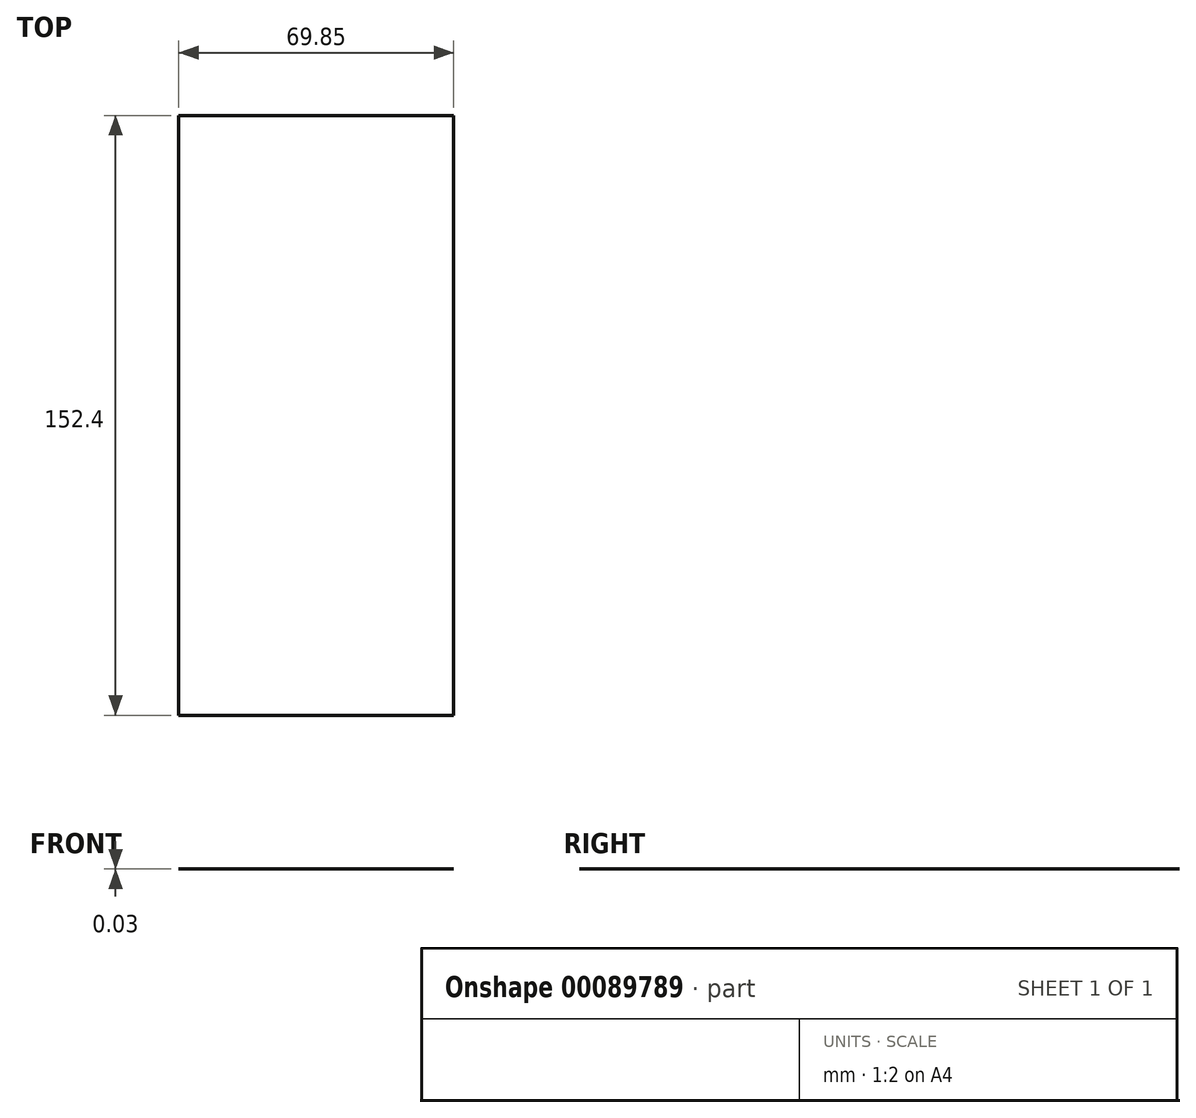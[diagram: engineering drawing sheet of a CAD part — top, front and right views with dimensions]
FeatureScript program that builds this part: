
annotation { "Feature Type Name" : "Feature", "Feature Type Description" : "" }
export const myFeature = defineFeature(function(context is Context, id is Id, definition is map)
    precondition{}
    {
        {
            var Q0;
            Q0=qCreatedBy(makeId("Top.planeOp"),FACE);
            var sketch = newSketch(context, id + "F0", { "sketchPlane" : qUnion([Q0])});
            skLineSegment(sketch, "E0.bottom", {"start": v(-56.72, -76.5) * mm, "end": v(13.13, -76.5) * mm});
            skLineSegment(sketch, "E0.top", {"start": v(-56.72, 75.9) * mm, "end": v(13.13, 75.9) * mm});
            skLineSegment(sketch, "E0.left", {"start": v(-56.72, -76.5) * mm, "end": v(-56.72, 75.9) * mm});
            skLineSegment(sketch, "E0.right", {"start": v(13.13, -76.5) * mm, "end": v(13.13, 75.9) * mm});
            skSolve(sketch);
        }
        {
            var Q0;
            Q0=makeQuery(id+"F0.imprint","IMPRINT",FACE,{"disambiguationData":[TD([[makeQuery(id+"F0.imprint","IMPRINT",EDGE,{"derivedFrom":sQuery(id+"F0.wireOp",EDGE,"E0.bottom")}),1.0]])]});
            extrude(context, id + "F1", {"entities" : qUnion([Q0]), "depth" : 0.03 * mm});
        }
    });
